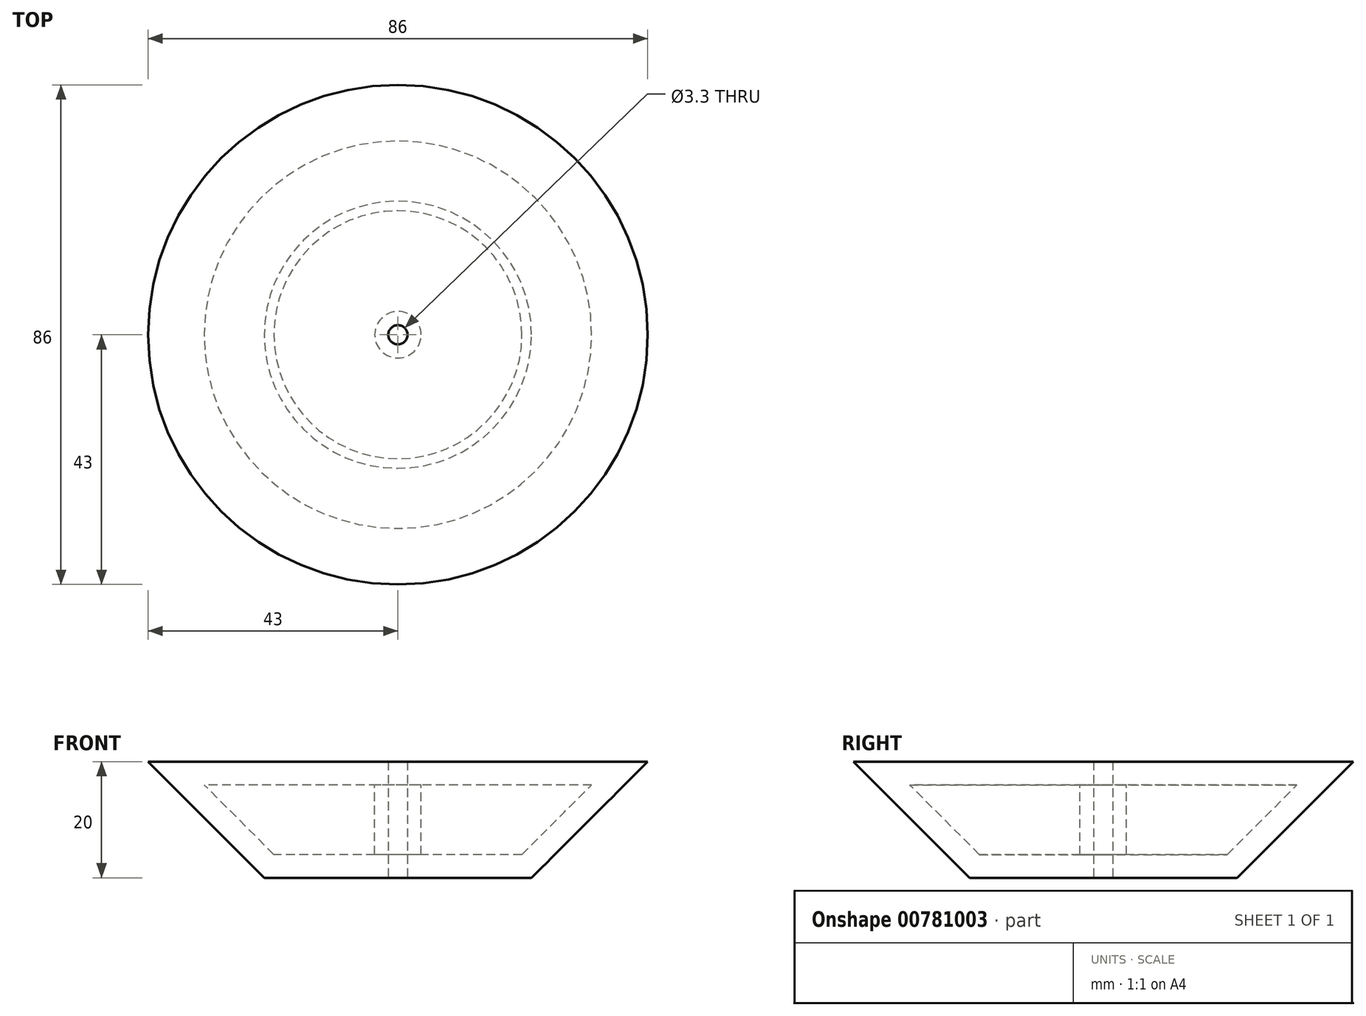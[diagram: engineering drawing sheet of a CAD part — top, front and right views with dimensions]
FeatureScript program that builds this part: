
annotation { "Feature Type Name" : "Feature", "Feature Type Description" : "" }
export const myFeature = defineFeature(function(context is Context, id is Id, definition is map)
    precondition{}
    {
        {
            var Q0;
            Q0=qCreatedBy(makeId("Front.planeOp"),FACE);
            var sketch = newSketch(context, id + "F0", { "sketchPlane" : qUnion([Q0])});
            skLineSegment(sketch, "E0.bottom", {"start": v(-43, 10) * mm, "end": v(0, 10) * mm});
            skLineSegment(sketch, "E0.top", {"start": v(-23, -10) * mm, "end": v(0, -10) * mm});
            skLineSegment(sketch, "E0.left", {"start": v(-43, 10) * mm, "end": v(-23, -10) * mm});
            skLineSegment(sketch, "E0.right", {"start": v(0, 10) * mm, "end": v(0, -10) * mm});
            skLineSegment(sketch, "E1.0", {"start": v(-33.34, 6) * mm, "end": v(-4, 6) * mm});
            skLineSegment(sketch, "E1.1", {"start": v(-33.34, 6) * mm, "end": v(-21.34, -6) * mm});
            skLineSegment(sketch, "E1.2", {"start": v(-21.34, -6) * mm, "end": v(-4, -6) * mm});
            skLineSegment(sketch, "E1.3", {"start": v(-4, 6) * mm, "end": v(-4, -6) * mm});
            skSolve(sketch);
        }
        {
            var Q0;
            Q0=makeQuery(id+"F0.imprint","IMPRINT",FACE,{"disambiguationData":[TD([[makeQuery(id+"F0.imprint","IMPRINT",EDGE,{"derivedFrom":sQuery(id+"F0.wireOp",EDGE,"E0.bottom")}),-1.0]])]});
            var Q1;
            Q1=sQuery(id+"F0.wireOp",EDGE,"E0.left");
            var Q2;
            Q2=sQuery(id+"F0.wireOp",EDGE,"E1.1");
            var Q3;
            Q3=sQuery(id+"F0.wireOp",EDGE,"E0.right");
            revolve(context, id + "F1", {"surfaceOperationType" : NewSurfaceOperationType.NEW, "entities" : qUnion([Q0]), "surfaceEntities" : qUnion([Q1, Q2]), "axis" : qUnion([Q3]), "revolveType" : RevolveType.FULL});
        }
        {
            var Q0;
            Q0=makeQuery(id+"F1.opRevolve","SWEPT_FACE",FACE,{"disambiguationData":[OSD([sQuery(id+"F0.wireOp",EDGE,"E0.top")])]});
            var sketch = newSketch(context, id + "F2", { "sketchPlane" : qUnion([Q0])});
            skCircle(sketch, "E2", {"center": v(0, 0) * mm, "radius": 2 * mm});
            skSolve(sketch);
        }
        {
            var Q0;
            Q0=sQuery(id+"F2.wireOp",VERTEX,"E2.center");
            var Q1;
            Q1=makeQuery(id+"F1.opRevolve","SWEPT_BODY",BODY,{"disambiguationData":[OSD([sQuery(id+"F0.wireOp",EDGE,"E0.bottom"),sQuery(id+"F0.wireOp",EDGE,"E0.top"),sQuery(id+"F0.wireOp",EDGE,"E0.left"),sQuery(id+"F0.wireOp",EDGE,"E0.right"),sQuery(id+"F0.wireOp",EDGE,"E1.0"),sQuery(id+"F0.wireOp",EDGE,"E1.1"),sQuery(id+"F0.wireOp",EDGE,"E1.2"),sQuery(id+"F0.wireOp",EDGE,"E1.3")])]});
            hole(context, id + "F3", {"style" : HoleStyle.SIMPLE, "endStyle" : HoleEndStyle.THROUGH, "standardTappedOrClearance" : lookupTablePath({ "standard" : "ISO", "engagement" : "75%", "pitch" : "0.7 mm", "size" : "M4", "type" : "Tapped" }), "standardBlindInLast" : lookupTablePath({ "standard" : "ISO", "engagement" : "75%", "pitch" : "0.7 mm", "size" : "M4", "type" : "Tapped" }), "holeDiameter" : 3.3 * mm, "majorDiameter" : 4 * mm, "showTappedDepth" : true, "isTappedThrough" : true, "tappedDepth" : 12 * mm, "tapClearance" : 3, "locations" : qUnion([Q0]), "scope" : qUnion([Q1])});
        }
    });
